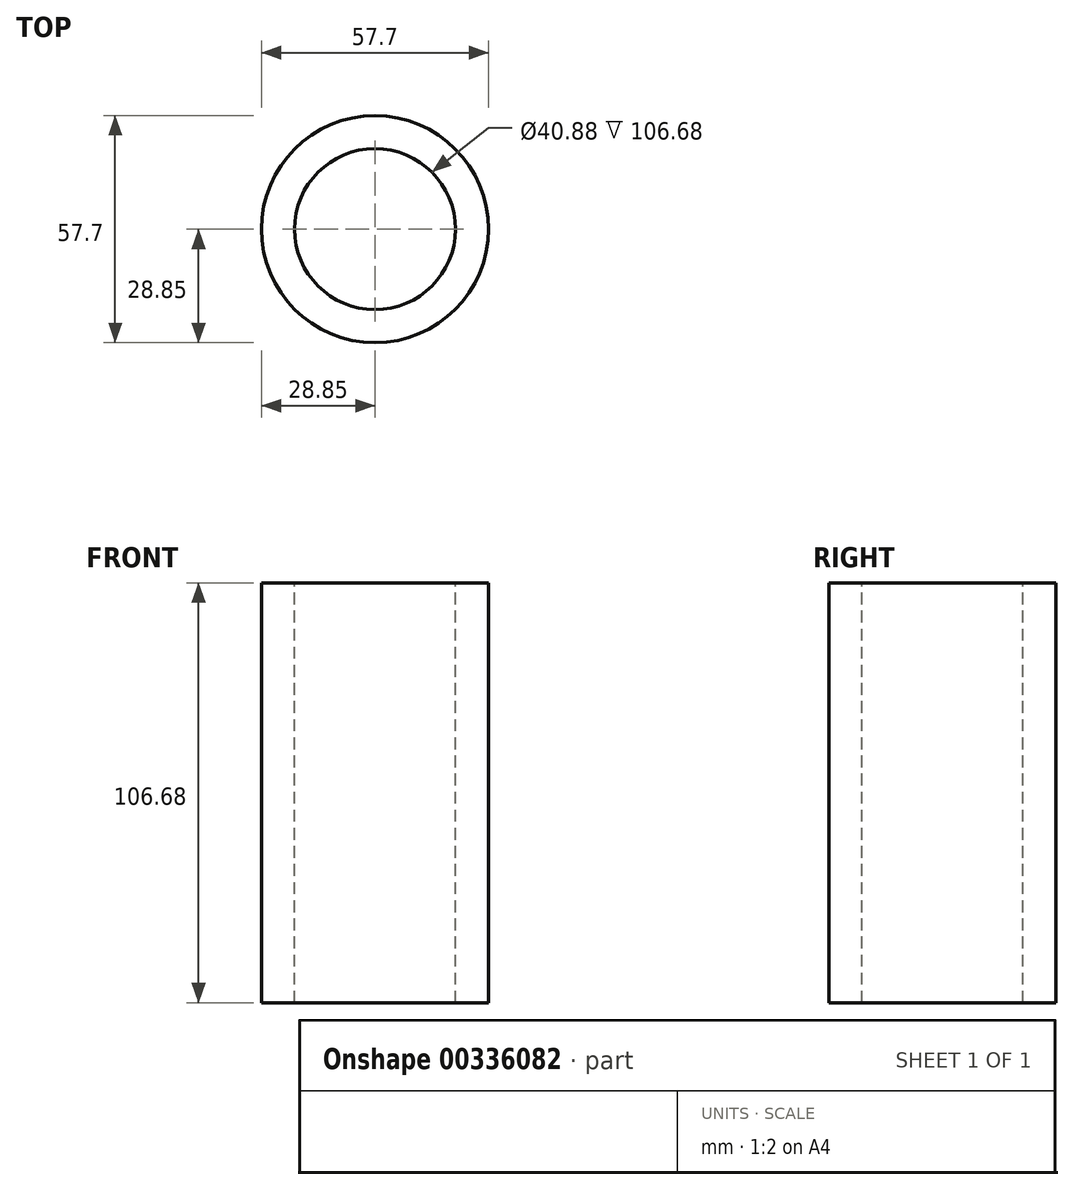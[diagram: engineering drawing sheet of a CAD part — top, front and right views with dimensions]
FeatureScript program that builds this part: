
annotation { "Feature Type Name" : "Feature", "Feature Type Description" : "" }
export const myFeature = defineFeature(function(context is Context, id is Id, definition is map)
    precondition{}
    {
        {
            var Q0;
            Q0=qCreatedBy(makeId("Top.planeOp"),FACE);
            var sketch = newSketch(context, id + "F0", { "sketchPlane" : qUnion([Q0])});
            skCircle(sketch, "E0", {"center": v(0, 0) * mm, "radius": 28.85 * mm});
            skLineSegment(sketch, "E1", {"start": v(0, 0) * mm, "end": v(-28.85, 0) * mm});
            skLineSegment(sketch, "E2", {"start": v(0, 0) * mm, "end": v(0, 28.85) * mm});
            skLineSegment(sketch, "E3", {"start": v(0, 0) * mm, "end": v(28.85, 0) * mm});
            skLineSegment(sketch, "E4", {"start": v(0, 0) * mm, "end": v(0, -28.85) * mm});
            skLineSegment(sketch, "E5", {"start": v(0, 0) * mm, "end": v(19.81, 20.97) * mm});
            skLineSegment(sketch, "E6", {"start": v(0, 0) * mm, "end": v(-20.97, 19.81) * mm});
            skLineSegment(sketch, "E7", {"start": v(0, 0) * mm, "end": v(-19.81, -20.97) * mm});
            skLineSegment(sketch, "E8", {"start": v(0, 0) * mm, "end": v(20.97, -19.81) * mm});
            skSolve(sketch);
        }
        {
            var Q0;
            Q0 = qSketchRegion(id + "F0", true);
            extrude(context, id + "F1", {"entities" : qUnion([Q0]), "depth" : 106.68 * mm});
        }
        {
            var Q0;
            Q0=makeQuery(id+"F1.opExtrude","CAP_FACE",FACE,{"disambiguationData":[OSD([sQuery(id+"F0.wireOp",EDGE,"E0")])],"isStart":false});
            var sketch = newSketch(context, id + "F2", { "sketchPlane" : qUnion([Q0])});
            skCircle(sketch, "E9", {"center": v(0, 0) * mm, "radius": 20.44 * mm});
            skSolve(sketch);
        }
        {
            var Q0;
            Q0 = qSketchRegion(id + "F2", true);
            extrude(context, id + "F3", {"entities" : qUnion([Q0]), "operationType" : NewBodyOperationType.REMOVE, "oppositeDirection" : true, "depth" : 151.13 * mm});
        }
    });
